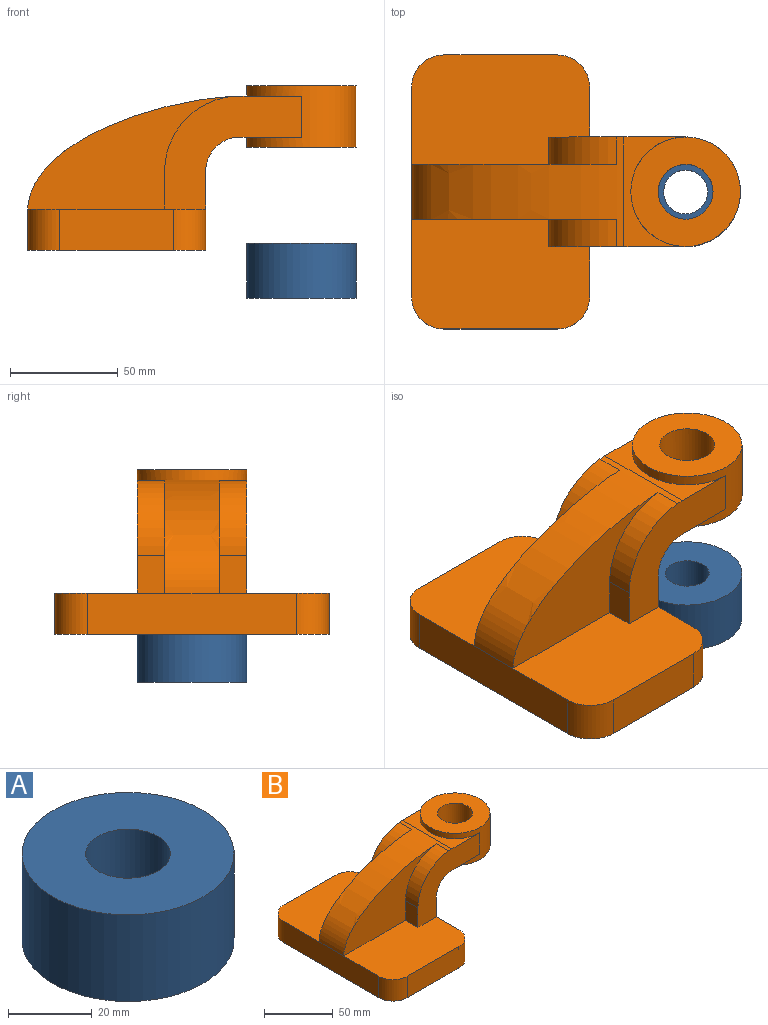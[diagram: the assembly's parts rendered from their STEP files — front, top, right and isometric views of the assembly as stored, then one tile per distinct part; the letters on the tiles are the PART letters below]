
ASSEMBLY  parts=2 mates=1
PART A: 4 faces, bbox 50.8x50.8x25.4 mm
  f0: cylinder r=25.4mm len=50.8mm, axis (0,0,1), area 4053.7mm2, adj f1,f2
  f1: plane 50.8x50.8mm, normal (0,0,1), area 1702.5mm2, adj f0,f3
  f2: plane 50.8x50.8mm, normal (0,0,-1), area 1702.5mm2, adj f0,f3
  f3: cylinder r=10.16mm len=25.4mm, axis (0,0,1), area 1621.5mm2, adj f1,f2
PART B: 27 faces, bbox 152.4x127x76.2 mm
  f0: plane 17.48x12.7mm, normal (-1,0,0), area 221.9mm2, adj f1,f2,f16,f18
  f1: plane 82.55x50.8mm, normal (0,0,1), area 3855mm2, adj f0,f4,f6,f8,f16,f18,f22,f23
  f2: cylinder r=34.92mm len=34.77mm, axis (0,1,0), area 655.2mm2, adj f0,f9,f16,f18
  f3: plane 82.55x50.8mm, normal (0,0,1), area 3855mm2, adj f4,f6,f7,f11,f15,f17,f24,f25
  f4: plane 97x19.05mm, normal (-1,0,0), area 1847.8mm2, adj f1,f3,f5,f9,f23,f25
  f5: plane 127x82.55mm, normal (0,0,-1), area 10290.7mm2, adj f4,f6,f7,f8,f22,f23,f24,f25
  f6: plane 97x36.53mm, normal (1,0,0), area 2735.6mm2, adj f1,f3,f5,f12,f15,f16,f22,f24
  f7: plane 52.55x19.05mm, normal (0,-1,0), area 1001.1mm2, adj f3,f5,f24,f25
  f8: plane 52.55x19.05mm, normal (0,1,0), area 1001.1mm2, adj f1,f5,f22,f23
  f9: extruded ~98.43x52.4mm, area 3110.9mm2, adj f2,f4,f10,f14,f15,f16,f17,f18
  f10: cylinder r=34.92mm len=34.77mm, axis (0,1,0), area 655.2mm2, adj f9,f11,f15,f17
  f11: plane 17.48x12.7mm, normal (-1,0,0), area 221.9mm2, adj f3,f10,f15,f17
  f12: cylinder r=15.88mm len=50.8mm, axis (0,1,0), area 1266.8mm2, adj f6,f13,f15,f16
  f13: plane 50.8x28.58mm, normal (0,0,-1), area 438.2mm2, adj f12,f15,f16,f19
  f14: plane 50.8x28.58mm, normal (0,0,1), area 438.2mm2, adj f9,f15,f16,f19
  f15: plane 63.5x52.4mm, normal (0,-1,0), area 1637.3mm2, adj f3,f6,f9,f10,f11,f12,f13,f14
  f16: plane 63.5x52.4mm, normal (0,1,0), area 1637.3mm2, adj f0,f1,f2,f6,f9,f12,f13,f14
  f17: plane 98.43x52.4mm, normal (0,-1,0), area 2298.4mm2, adj f3,f9,f10,f11
  f18: plane 98.43x52.4mm, normal (0,1,0), area 2298.4mm2, adj f0,f1,f2,f9
  f19: cylinder r=25.4mm len=50.8mm, axis (0,0,-1), area 3040.2mm2, adj f13,f14,f15,f16,f20,f21
  f20: plane 50.8x50.8mm, normal (0,0,-1), area 1520.1mm2, adj f19,f26
  f21: plane 50.8x50.8mm, normal (0,0,1), area 1520.1mm2, adj f19,f26
  f22: cylinder r=15mm len=19.05mm, axis (0,0,1), area 448.9mm2, adj f1,f5,f6,f8
  f23: cylinder r=15mm len=19.05mm, axis (0,0,-1), area 448.9mm2, adj f1,f4,f5,f8
  f24: cylinder r=15mm len=19.05mm, axis (0,0,-1), area 448.9mm2, adj f3,f5,f6,f7
  f25: cylinder r=15mm len=19.05mm, axis (0,0,1), area 448.9mm2, adj f3,f4,f5,f7
  f26: cylinder r=12.7mm len=28.58mm, axis (0,0,1), area 2280.2mm2, adj f20,f21
PLACE A t=(-29.94,50.32,-11.46)mm
PLACE B t=(-115.67,50.32,20.34)mm
MATE slider B.f19 <-> A.f0  axis (0,0,1) through (-29.94,50.32,87.02)mm
